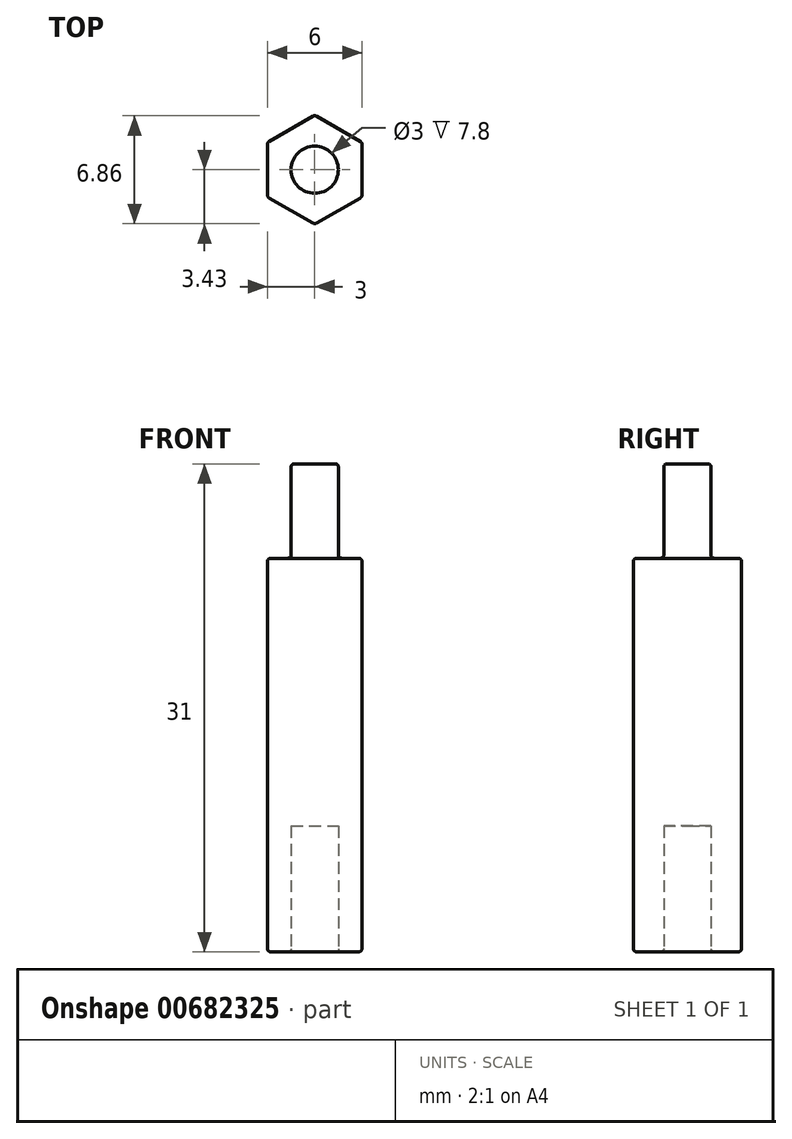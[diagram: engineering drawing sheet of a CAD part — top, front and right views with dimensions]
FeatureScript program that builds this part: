
annotation { "Feature Type Name" : "Feature", "Feature Type Description" : "" }
export const myFeature = defineFeature(function(context is Context, id is Id, definition is map)
    precondition{}
    {
        {
            var Q0;
            Q0=qCreatedBy(makeId("Top.planeOp"),FACE);
            var sketch = newSketch(context, id + "F0", { "sketchPlane" : qUnion([Q0])});
            skCircle(sketch, "E0.cCircle", {"center": v(0, 0) * mm, "radius": 3 * mm, "construction": true});
            skLineSegment(sketch, "E0.0", {"start": v(0, 3.46) * mm, "end": v(3, 1.73) * mm});
            skLineSegment(sketch, "E0.1", {"start": v(3, 1.73) * mm, "end": v(3, -1.73) * mm});
            skLineSegment(sketch, "E0.2", {"start": v(3, -1.73) * mm, "end": v(0, -3.46) * mm});
            skLineSegment(sketch, "E0.3", {"start": v(0, -3.46) * mm, "end": v(-3, -1.73) * mm});
            skLineSegment(sketch, "E0.4", {"start": v(-3, -1.73) * mm, "end": v(-3, 1.73) * mm});
            skLineSegment(sketch, "E0.5", {"start": v(-3, 1.73) * mm, "end": v(0, 3.46) * mm});
            skPoint(sketch, "E0.0.midPoint", {"position": v(1.5, 2.6) * mm});
            skSolve(sketch);
        }
        {
            var Q0;
            Q0 = qSketchRegion(id + "F0", true);
            extrude(context, id + "F1", {"entities" : qUnion([Q0]), "depth" : 25 * mm, "offsetDistance" : 25 * mm});
        }
        {
            var Q0;
            Q0=makeQuery(id+"F1.opExtrude","CAP_FACE",FACE,{"disambiguationData":[OSD([sQuery(id+"F0.wireOp",EDGE,"E0.0"),sQuery(id+"F0.wireOp",EDGE,"E0.1"),sQuery(id+"F0.wireOp",EDGE,"E0.2"),sQuery(id+"F0.wireOp",EDGE,"E0.3"),sQuery(id+"F0.wireOp",EDGE,"E0.4"),sQuery(id+"F0.wireOp",EDGE,"E0.5")])],"isStart":false});
            var sketch = newSketch(context, id + "F2", { "sketchPlane" : qUnion([Q0])});
            skCircle(sketch, "E1", {"center": v(0, 0) * mm, "radius": 1.5 * mm});
            skSolve(sketch);
        }
        {
            var Q0;
            Q0 = qSketchRegion(id + "F2", true);
            extrude(context, id + "F3", {"entities" : qUnion([Q0]), "operationType" : NewBodyOperationType.ADD, "depth" : 6 * mm, "offsetDistance" : 25 * mm});
        }
        {
            var Q0;
            Q0=makeQuery(id+"F1.opExtrude","CAP_FACE",FACE,{"disambiguationData":[OSD([sQuery(id+"F0.wireOp",EDGE,"E0.0"),sQuery(id+"F0.wireOp",EDGE,"E0.1"),sQuery(id+"F0.wireOp",EDGE,"E0.2"),sQuery(id+"F0.wireOp",EDGE,"E0.3"),sQuery(id+"F0.wireOp",EDGE,"E0.4"),sQuery(id+"F0.wireOp",EDGE,"E0.5")])],"isStart":true});
            var sketch = newSketch(context, id + "F4", { "sketchPlane" : qUnion([Q0])});
            skCircle(sketch, "E2", {"center": v(0, 0) * mm, "radius": 1.5 * mm});
            skSolve(sketch);
        }
        {
            var Q0;
            Q0 = qSketchRegion(id + "F4", true);
            extrude(context, id + "F5", {"entities" : qUnion([Q0]), "operationType" : NewBodyOperationType.REMOVE, "oppositeDirection" : true, "depth" : 8 * mm, "offsetDistance" : 25 * mm});
        }
        {
            var Q0;
            Q0=makeQuery(id+"F1.opExtrude","CAP_FACE",FACE,{"disambiguationData":[OSD([sQuery(id+"F0.wireOp",EDGE,"E0.0"),sQuery(id+"F0.wireOp",EDGE,"E0.1"),sQuery(id+"F0.wireOp",EDGE,"E0.2"),sQuery(id+"F0.wireOp",EDGE,"E0.3"),sQuery(id+"F0.wireOp",EDGE,"E0.4"),sQuery(id+"F0.wireOp",EDGE,"E0.5")])],"isStart":true});
            var Q1;
            Q1=makeQuery(id+"F1.opExtrude","CAP_FACE",FACE,{"disambiguationData":[OSD([sQuery(id+"F0.wireOp",EDGE,"E0.0"),sQuery(id+"F0.wireOp",EDGE,"E0.1"),sQuery(id+"F0.wireOp",EDGE,"E0.2"),sQuery(id+"F0.wireOp",EDGE,"E0.3"),sQuery(id+"F0.wireOp",EDGE,"E0.4"),sQuery(id+"F0.wireOp",EDGE,"E0.5")])],"isStart":false});
            var Q2;
            Q2=makeQuery(id+"F3.opExtrude","CAP_FACE",FACE,{"disambiguationData":[OSD([sQuery(id+"F2.wireOp",EDGE,"E1")])],"isStart":false});
            var Q3;
            Q3=makeQuery(id+"F1.opExtrude","SWEPT_FACE",FACE,{"disambiguationData":[OSD([sQuery(id+"F0.wireOp",EDGE,"E0.3")])]});
            var Q4;
            Q4=makeQuery(id+"F1.opExtrude","SWEPT_FACE",FACE,{"disambiguationData":[OSD([sQuery(id+"F0.wireOp",EDGE,"E0.4")])]});
            var Q5;
            Q5=makeQuery(id+"F1.opExtrude","SWEPT_FACE",FACE,{"disambiguationData":[OSD([sQuery(id+"F0.wireOp",EDGE,"E0.5")])]});
            var Q6;
            Q6=makeQuery(id+"F1.opExtrude","SWEPT_FACE",FACE,{"disambiguationData":[OSD([sQuery(id+"F0.wireOp",EDGE,"E0.0")])]});
            var Q7;
            Q7=makeQuery(id+"F1.opExtrude","SWEPT_FACE",FACE,{"disambiguationData":[OSD([sQuery(id+"F0.wireOp",EDGE,"E0.1")])]});
            fillet(context, id + "F6", {"entities" : qUnion([Q0, Q1, Q2, Q3, Q4, Q5, Q6, Q7]), "radius" : .2 * mm, "tangentPropagation" : true, "allowEdgeOverflow" : false});
        }
    });
